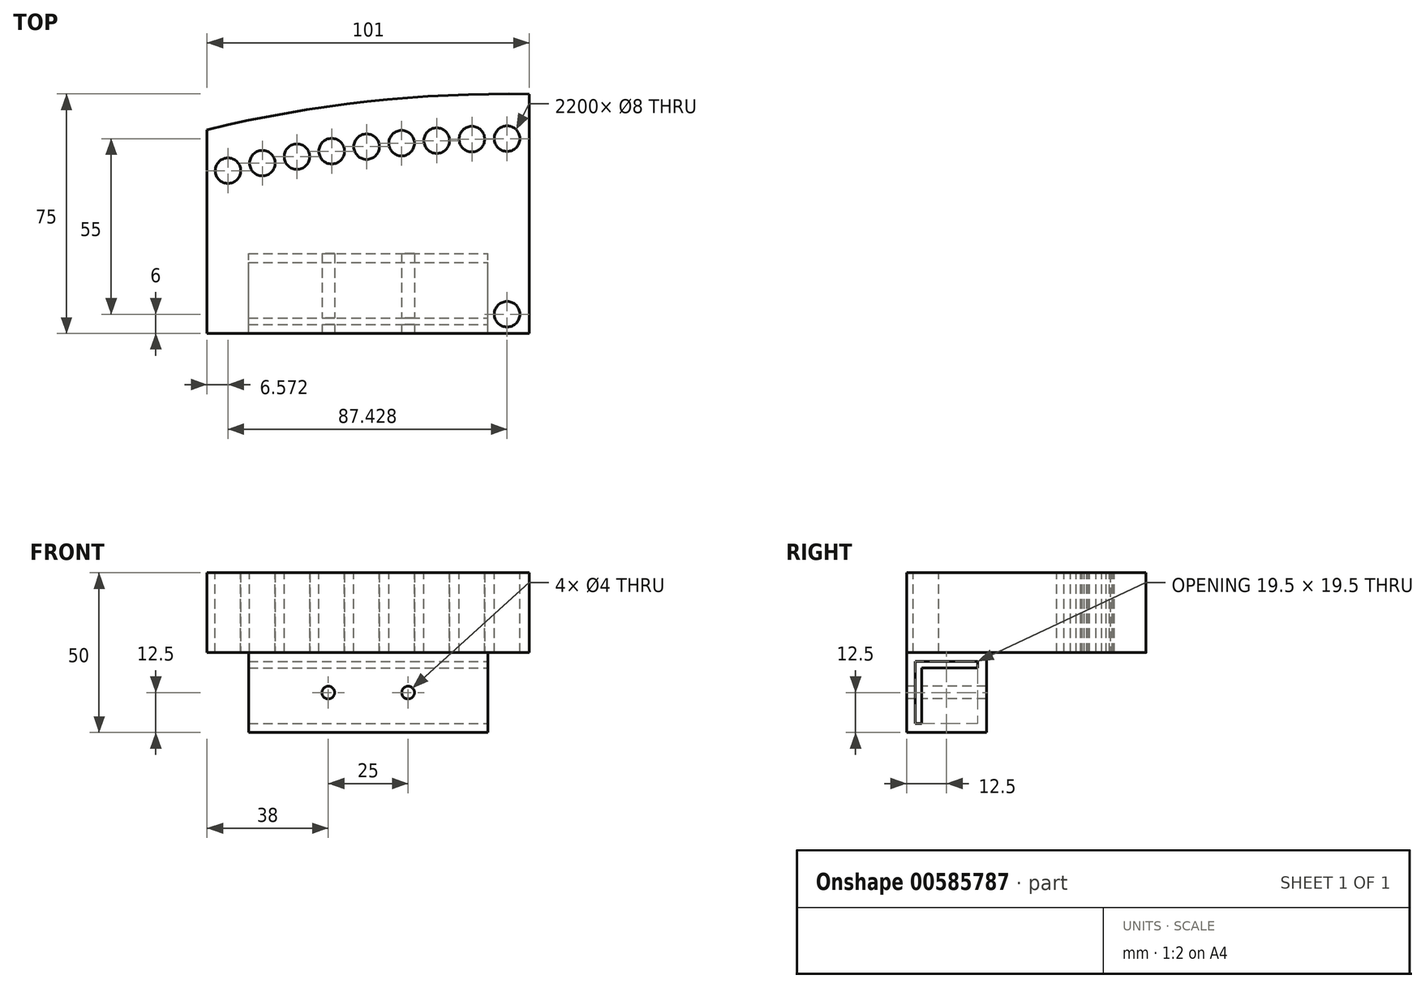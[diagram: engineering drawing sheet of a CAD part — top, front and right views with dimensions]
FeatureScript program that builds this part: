
annotation { "Feature Type Name" : "Feature", "Feature Type Description" : "" }
export const myFeature = defineFeature(function(context is Context, id is Id, definition is map)
    precondition{}
    {
        {
            var Q0;
            Q0=qCreatedBy(makeId("Top.planeOp"),FACE);
            var sketch = newSketch(context, id + "F0", { "sketchPlane" : qUnion([Q0])});
            skCircle(sketch, "E0", {"center": v(0, 0) * mm, "radius": 400 * mm});
            skCircle(sketch, "E1", {"center": v(0, 386) * mm, "radius": 4 * mm});
            skSolve(sketch);
        }
        {
            var Q0;
            Q0=makeQuery(id+"F0.imprint","IMPRINT",FACE,{"disambiguationData":[TD([[makeQuery(id+"F0.imprint","IMPRINT",EDGE,{"derivedFrom":sQuery(id+"F0.wireOp",EDGE,"E0")}),1.0]])]});
            extrude(context, id + "F1", {"entities" : qUnion([Q0]), "depth" : 25 * mm, "offsetDistance" : 25 * mm});
        }
        {
            var Q0;
            Q0=makeQuery(id+"F1.opExtrude","CAP_FACE",FACE,{"disambiguationData":[OSD([sQuery(id+"F0.wireOp",EDGE,"E0"),sQuery(id+"F0.wireOp",EDGE,"E1")])],"isStart":false});
            var sketch = newSketch(context, id + "F2", { "sketchPlane" : qUnion([Q0])});
            skCircle(sketch, "E2", {"center": v(0, 0) * mm, "radius": 12.88 * mm});
            skSolve(sketch);
        }
        {
            var Q0;
            Q0=makeQuery(id+"F1.opExtrude","SWEPT_BODY",BODY,{"disambiguationData":[OSD([sQuery(id+"F0.wireOp",EDGE,"E0"),sQuery(id+"F0.wireOp",EDGE,"E1")])]});
            var Q1;
            Q1=sQuery(id+"F2.wireOp",EDGE,"E2");
            circularPattern(context, id + "F3", {"entities" : qUnion([Q0]), "axis" : qUnion([Q1]), "angle" : 360 * degree, "instanceCount" : 220, "equalSpace" : true});
        }
        {
            var Q0;
            Q0=makeQuery(id+"F3.opPattern","COPY",FACE,{"derivedFrom":makeQuery(id+"F1.opExtrude","CAP_FACE",FACE,{"disambiguationData":[OSD([sQuery(id+"F0.wireOp",EDGE,"E0"),sQuery(id+"F0.wireOp",EDGE,"E1")])],"isStart":false}),"instanceName":"1"});
            var sketch = newSketch(context, id + "F4", { "sketchPlane" : qUnion([Q0])});
            skLineSegment(sketch, "E3.bottom", {"start": v(0, 325) * mm, "end": v(-100, 325) * mm});
            skLineSegment(sketch, "E3.top", {"start": v(0, 400) * mm, "end": v(-100, 400) * mm});
            skLineSegment(sketch, "E3.left", {"start": v(0, 325) * mm, "end": v(0, 400) * mm});
            skLineSegment(sketch, "E3.right", {"start": v(-100, 325) * mm, "end": v(-100, 400) * mm});
            skLineSegment(sketch, "E4.bottom", {"start": v(0, 325) * mm, "end": v(100, 325) * mm});
            skLineSegment(sketch, "E4.top", {"start": v(0, 400) * mm, "end": v(100, 400) * mm});
            skLineSegment(sketch, "E4.right", {"start": v(100, 325) * mm, "end": v(100, 400) * mm});
            skSolve(sketch);
        }
        {
            var Q0;
            {var subQ5=sQuery(id+"F4.wireOp",EDGE,"E3.bottom");Q0=makeQuery(id+"F4.imprint","IMPRINT",FACE,{"disambiguationData":[TD([[makeQuery(id+"F4.imprint","IMPRINT",EDGE,{"derivedFrom":subQ5}),1.0]])]});}
            var sketch = newSketch(context, id + "F5", { "sketchPlane" : qUnion([Q0])});
            skSolve(sketch);
        }
        {
            var Q0;
            {var subQ5=sQuery(id+"F4.wireOp",EDGE,"E3.bottom");Q0=makeQuery(id+"F5.imprint","IMPRINT",FACE,{"disambiguationData":[TD([[makeQuery(id+"F5.imprint","IMPRINT",EDGE,{"derivedFrom":makeQuery(id+"F4.imprint","IMPRINT",EDGE,{"derivedFrom":subQ5})}),1.0]])]});}
            extrude(context, id + "F6", {"entities" : qUnion([Q0]), "operationType" : NewBodyOperationType.REMOVE, "oppositeDirection" : true, "depth" : 25 * mm, "offsetDistance" : 25 * mm});
        }
        {
            var Q0;
            {var subQ0=sQuery(id+"F4.wireOp",EDGE,"E4.bottom");Q0=makeQuery(id+"F4.imprint","IMPRINT",FACE,{"disambiguationData":[TD([[makeQuery(id+"F4.imprint","IMPRINT",EDGE,{"derivedFrom":subQ0}),1.0]])]});}
            var sketch = newSketch(context, id + "F7", { "sketchPlane" : qUnion([Q0])});
            skCircle(sketch, "E5.0", {"center": v(11.02, 385.84) * mm, "radius": 4 * mm});
            skCircle(sketch, "E6.0", {"center": v(0, 386) * mm, "radius": 4 * mm});
            skCircle(sketch, "E6.1", {"center": v(-11.02, 385.84) * mm, "radius": 4 * mm});
            skCircle(sketch, "E6.2", {"center": v(-22.04, 385.37) * mm, "radius": 4 * mm});
            skCircle(sketch, "E6.3", {"center": v(-33.03, 384.58) * mm, "radius": 4 * mm});
            skCircle(sketch, "E6.4", {"center": v(-44, 383.48) * mm, "radius": 4 * mm});
            skCircle(sketch, "E6.5", {"center": v(-54.93, 382.07) * mm, "radius": 4 * mm});
            skCircle(sketch, "E6.6", {"center": v(-65.82, 380.35) * mm, "radius": 4 * mm});
            skCircle(sketch, "E6.7", {"center": v(-76.66, 378.31) * mm, "radius": 4 * mm});
            skCircle(sketch, "E6.8", {"center": v(-87.43, 375.97) * mm, "radius": 4 * mm});
            skCircle(sketch, "E6.9", {"center": v(22.04, 385.37) * mm, "radius": 4 * mm});
            skCircle(sketch, "E6.10", {"center": v(33.03, 384.58) * mm, "radius": 4 * mm});
            skCircle(sketch, "E6.11", {"center": v(44, 383.48) * mm, "radius": 4 * mm});
            skCircle(sketch, "E6.12", {"center": v(54.93, 382.07) * mm, "radius": 4 * mm});
            skCircle(sketch, "E6.13", {"center": v(65.82, 380.35) * mm, "radius": 4 * mm});
            skCircle(sketch, "E6.14", {"center": v(76.66, 378.31) * mm, "radius": 4 * mm});
            skCircle(sketch, "E6.15", {"center": v(87.43, 375.97) * mm, "radius": 4 * mm});
            skSolve(sketch);
        }
        {
            var Q0;
            Q0 = qSketchRegion(id + "F7", true);
            var Q1;
            Q1 = qSketchRegion(id + "F7", true);
            extrude(context, id + "F8", {"entities" : qUnion([Q0, Q1]), "operationType" : NewBodyOperationType.REMOVE, "oppositeDirection" : true, "depth" : 25 * mm, "offsetDistance" : 25 * mm});
        }
        {
            var Q0;
            {var subQ2=sQuery(id+"F4.wireOp",EDGE,"E3.bottom");Q0=makeQuery(id+"F4.imprint","IMPRINT",FACE,{"disambiguationData":[TD([[makeQuery(id+"F4.imprint","IMPRINT",EDGE,{"derivedFrom":subQ2}),-1.0]])]});}
            var sketch = newSketch(context, id + "F9", { "sketchPlane" : qUnion([Q0])});
            skLineSegment(sketch, "E7.bottom", {"start": v(7, 325) * mm, "end": v(-93, 325) * mm});
            skLineSegment(sketch, "E7.top", {"start": v(7, 400) * mm, "end": v(-93, 400) * mm});
            skLineSegment(sketch, "E7.left", {"start": v(7, 325) * mm, "end": v(7, 400) * mm});
            skLineSegment(sketch, "E7.right", {"start": v(-93, 325) * mm, "end": v(-93, 400) * mm});
            skCircle(sketch, "E8", {"center": v(0, 331) * mm, "radius": 4 * mm});
            skSolve(sketch);
        }
        {
            var Q0;
            {var subQ5=sQuery(id+"F4.wireOp",EDGE,"E3.bottom");Q0=makeQuery(id+"F4.imprint","IMPRINT",FACE,{"disambiguationData":[TD([[makeQuery(id+"F4.imprint","IMPRINT",EDGE,{"derivedFrom":subQ5}),1.0]])]});}
            var sketch = newSketch(context, id + "F10", { "sketchPlane" : qUnion([Q0])});
            skCircle(sketch, "E9.0", {"center": v(0, 331) * mm, "radius": 4 * mm});
            skSolve(sketch);
        }
        {
            var Q0;
            Q0 = qSketchRegion(id + "F10", true);
            extrude(context, id + "F11", {"entities" : qUnion([Q0]), "operationType" : NewBodyOperationType.REMOVE, "oppositeDirection" : true, "depth" : 25 * mm, "offsetDistance" : 25 * mm});
        }
        {
            var Q0;
            Q0=makeQuery(id+"F9.imprint","IMPRINT",FACE,{"disambiguationData":[TD([[makeQuery(id+"F9.imprint","IMPRINT",EDGE,{"derivedFrom":makeQuery(id+"F4.imprint","IMPRINT",EDGE,{"derivedFrom":makeQuery(id+"F3.opPattern","COPY",EDGE,{"derivedFrom":makeQuery(id+"F1.opExtrude","CAP_EDGE",EDGE,{"disambiguationData":[OSD([sQuery(id+"F0.wireOp",EDGE,"E1")])],"isStart":false}),"instanceName":"1"})})}),-1.0]])]});
            var sketch = newSketch(context, id + "F12", { "sketchPlane" : qUnion([Q0])});
            skLineSegment(sketch, "E10.0.0", {"start": v(-100, 325) * mm, "end": v(-93, 325) * mm});
            skLineSegment(sketch, "E10.0.1", {"start": v(-93, 325) * mm, "end": v(-93, 389.04) * mm});
            skArc(sketch, "E10.0.2", {"start": v(-93, 389.04) * mm, "mid": v(-96.5, 388.18) * mm, "end": v(-100, 387.3) * mm});
            skLineSegment(sketch, "E10.0.3", {"start": v(-100, 387.3) * mm, "end": v(-100, 325) * mm});
            skLineSegment(sketch, "E11.0.0", {"start": v(7, 400) * mm, "end": v(7, 325) * mm});
            skLineSegment(sketch, "E11.0.1", {"start": v(0, 325) * mm, "end": v(100, 325) * mm});
            skLineSegment(sketch, "E11.0.2", {"start": v(100, 325) * mm, "end": v(100, 387.3) * mm});
            skArc(sketch, "E11.0.3", {"start": v(100, 387.3) * mm, "mid": v(50.4, 396.81) * mm, "end": v(0, 400) * mm});
            skSolve(sketch);
        }
        {
            var Q0;
            {var subQ0=sQuery(id+"F4.wireOp",EDGE,"E4.bottom");Q0=makeQuery(id+"F4.imprint","IMPRINT",FACE,{"disambiguationData":[TD([[makeQuery(id+"F4.imprint","IMPRINT",EDGE,{"derivedFrom":subQ0}),1.0]])]});}
            var sketch = newSketch(context, id + "F13", { "sketchPlane" : qUnion([Q0])});
            skLineSegment(sketch, "E12.bottom", {"start": v(7, 411.47) * mm, "end": v(107, 411.47) * mm});
            skLineSegment(sketch, "E12.top", {"start": v(7, 321.47) * mm, "end": v(107, 321.47) * mm});
            skLineSegment(sketch, "E12.left", {"start": v(7, 411.47) * mm, "end": v(7, 321.47) * mm});
            skLineSegment(sketch, "E12.right", {"start": v(107, 411.47) * mm, "end": v(107, 321.47) * mm});
            skSolve(sketch);
        }
        {
            var Q0;
            Q0 = qSketchRegion(id + "F13", true);
            extrude(context, id + "F14", {"entities" : qUnion([Q0]), "operationType" : NewBodyOperationType.REMOVE, "oppositeDirection" : true, "depth" : 25 * mm, "offsetDistance" : 25 * mm});
        }
        {
            var Q0;
            {var subQ2=sQuery(id+"F4.wireOp",EDGE,"E3.bottom");Q0=makeQuery(id+"F4.imprint","IMPRINT",FACE,{"disambiguationData":[TD([[makeQuery(id+"F4.imprint","IMPRINT",EDGE,{"derivedFrom":subQ2}),-1.0]])]});}
            var sketch = newSketch(context, id + "F15", { "sketchPlane" : qUnion([Q0])});
            skLineSegment(sketch, "E13.bottom", {"start": v(-100, 325) * mm, "end": v(-94, 325) * mm});
            skLineSegment(sketch, "E13.top", {"start": v(-100, 393.92) * mm, "end": v(-94, 393.92) * mm});
            skLineSegment(sketch, "E13.left", {"start": v(-100, 325) * mm, "end": v(-100, 393.92) * mm});
            skLineSegment(sketch, "E13.right", {"start": v(-94, 325) * mm, "end": v(-94, 393.92) * mm});
            skSolve(sketch);
        }
        {
            var Q0;
            Q0 = qSketchRegion(id + "F15", true);
            var Q1;
            Q1 = qSketchRegion(id + "F15", true);
            extrude(context, id + "F16", {"entities" : qUnion([Q0, Q1]), "operationType" : NewBodyOperationType.REMOVE, "oppositeDirection" : true, "depth" : 25 * mm, "offsetDistance" : 25 * mm});
        }
        {
            var Q0;
            Q0=makeQuery(id+"F3.opPattern","COPY",FACE,{"derivedFrom":makeQuery(id+"F1.opExtrude","CAP_FACE",FACE,{"disambiguationData":[OSD([sQuery(id+"F0.wireOp",EDGE,"E0"),sQuery(id+"F0.wireOp",EDGE,"E1")])],"isStart":true}),"instanceName":"74"});
            var sketch = newSketch(context, id + "F17", { "sketchPlane" : qUnion([Q0])});
            skLineSegment(sketch, "E14.bottom", {"start": v(-81, -325) * mm, "end": v(-6, -325) * mm});
            skLineSegment(sketch, "E14.top", {"start": v(-81, -350) * mm, "end": v(-6, -350) * mm});
            skLineSegment(sketch, "E14.left", {"start": v(-81, -325) * mm, "end": v(-81, -350) * mm});
            skLineSegment(sketch, "E14.right", {"start": v(-6, -325) * mm, "end": v(-6, -350) * mm});
            skSolve(sketch);
        }
        {
            var Q0;
            Q0 = qSketchRegion(id + "F17", true);
            extrude(context, id + "F18", {"entities" : qUnion([Q0]), "depth" : 25 * mm, "offsetDistance" : 25 * mm});
        }
        {
            var Q0;
            Q0=makeQuery(id+"F18.opExtrude","SWEPT_FACE",FACE,{"disambiguationData":[OSD([sQuery(id+"F17.wireOp",EDGE,"E14.right")])]});
            var sketch = newSketch(context, id + "F19", { "sketchPlane" : qUnion([Q0])});
            skLineSegment(sketch, "E15.bottom", {"start": v(327.75, -4.75) * mm, "end": v(347.25, -4.75) * mm});
            skLineSegment(sketch, "E15.top", {"start": v(327.75, -2.75) * mm, "end": v(347.25, -2.75) * mm});
            skLineSegment(sketch, "E15.left", {"start": v(327.75, -2.75) * mm, "end": v(327.75, -4.75) * mm});
            skLineSegment(sketch, "E15.right", {"start": v(347.25, -2.75) * mm, "end": v(347.25, -4.75) * mm});
            skLineSegment(sketch, "E16.bottom", {"start": v(327.75, -4.75) * mm, "end": v(329.75, -4.75) * mm});
            skLineSegment(sketch, "E16.top", {"start": v(327.75, -22.25) * mm, "end": v(329.75, -22.25) * mm});
            skLineSegment(sketch, "E16.left", {"start": v(327.75, -4.75) * mm, "end": v(327.75, -22.25) * mm});
            skLineSegment(sketch, "E16.right", {"start": v(329.75, -4.75) * mm, "end": v(329.75, -22.25) * mm});
            skSolve(sketch);
        }
        {
            var Q0;
            Q0 = qSketchRegion(id + "F19", true);
            extrude(context, id + "F20", {"entities" : qUnion([Q0]), "operationType" : NewBodyOperationType.REMOVE, "oppositeDirection" : true, "depth" : 75 * mm, "offsetDistance" : 25 * mm});
        }
        {
            var Q0;
            Q0=makeQuery(id+"F18.opExtrude","SWEPT_FACE",FACE,{"disambiguationData":[OSD([sQuery(id+"F17.wireOp",EDGE,"E14.bottom")])]});
            var sketch = newSketch(context, id + "F21", { "sketchPlane" : qUnion([Q0])});
            skCircle(sketch, "E17", {"center": v(-56, -12.5) * mm, "radius": 2 * mm});
            skCircle(sketch, "E18", {"center": v(-31, -12.5) * mm, "radius": 2 * mm});
            skSolve(sketch);
        }
        {
            var Q0;
            Q0 = qSketchRegion(id + "F21", true);
            extrude(context, id + "F22", {"entities" : qUnion([Q0]), "operationType" : NewBodyOperationType.REMOVE, "oppositeDirection" : true, "depth" : 25 * mm, "offsetDistance" : 25 * mm});
        }
    });
